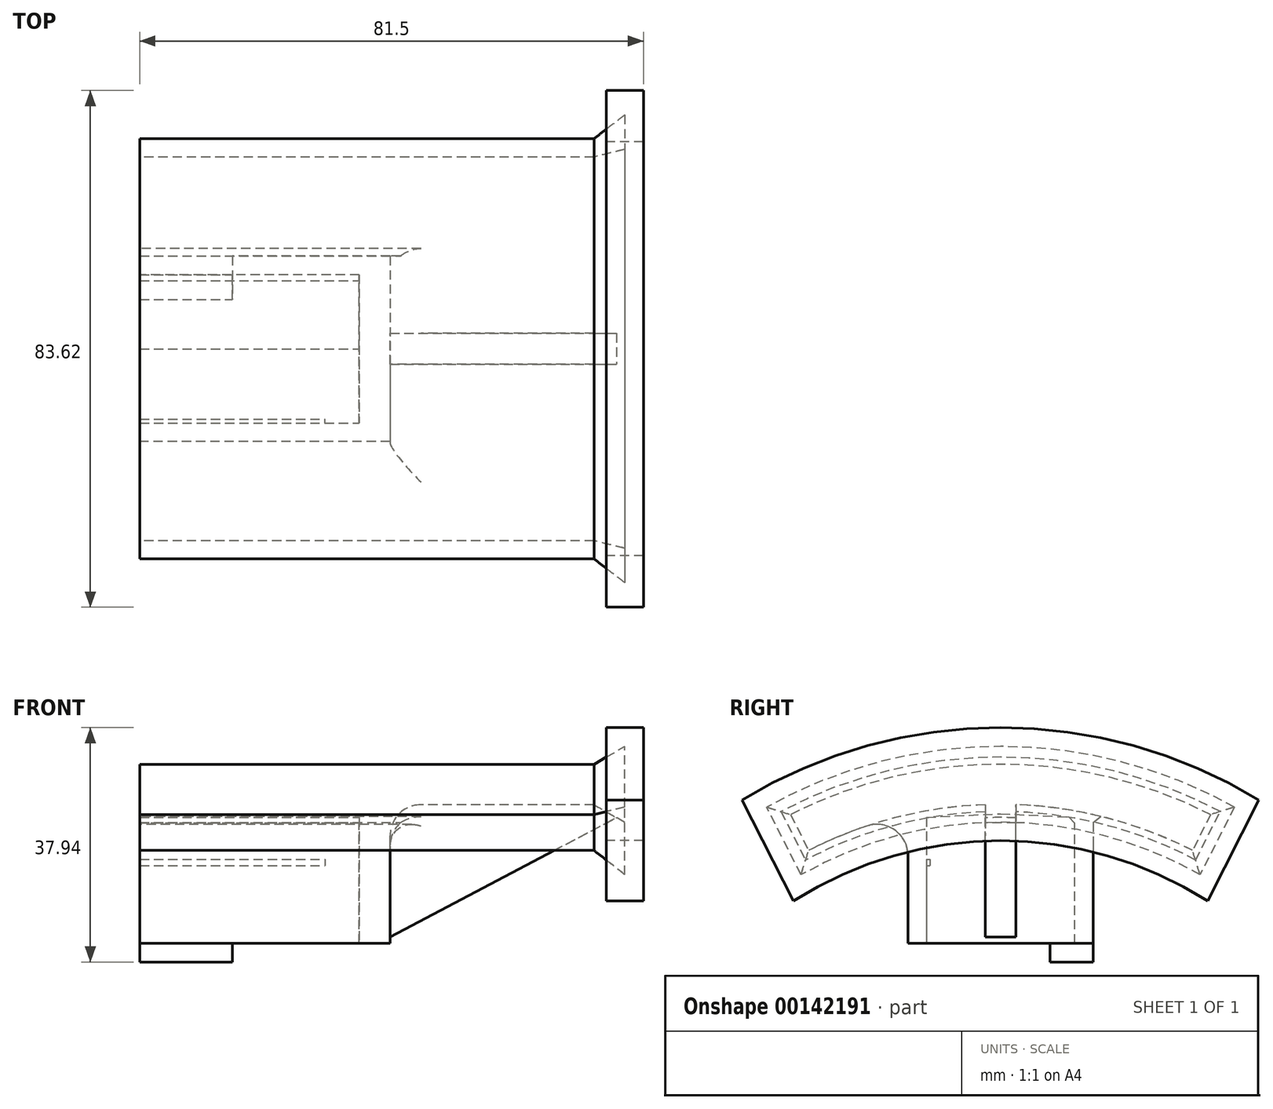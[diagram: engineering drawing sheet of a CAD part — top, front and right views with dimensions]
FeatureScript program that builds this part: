
annotation { "Feature Type Name" : "Feature", "Feature Type Description" : "" }
export const myFeature = defineFeature(function(context is Context, id is Id, definition is map)
    precondition{}
    {
        {
            var Q0;
            Q0=qCreatedBy(makeId("Right.planeOp"),FACE);
            var sketch = newSketch(context, id + "F0", { "sketchPlane" : qUnion([Q0])});
            skLineSegment(sketch, "E0", {"start": v(0, 0) * mm, "end": v(0, -27) * mm});
            skLineSegment(sketch, "E1", {"start": v(0, -27) * mm, "end": v(-7, -27) * mm});
            skLineSegment(sketch, "E2", {"start": v(-7, -27) * mm, "end": v(-7, -24) * mm});
            skLineSegment(sketch, "E3", {"start": v(-7, -24) * mm, "end": v(-3, -24) * mm});
            skLineSegment(sketch, "E4", {"start": v(-3, -24) * mm, "end": v(-3, -3) * mm});
            skLineSegment(sketch, "E5", {"start": v(-3, -3) * mm, "end": v(-27, -3) * mm});
            skLineSegment(sketch, "E6", {"start": v(-27, -3) * mm, "end": v(-27, -24) * mm});
            skLineSegment(sketch, "E7", {"start": v(-27, -24) * mm, "end": v(-30, -24) * mm});
            skLineSegment(sketch, "E8", {"start": v(-30, -24) * mm, "end": v(-30, 0) * mm});
            skLineSegment(sketch, "E9", {"start": v(-30, 0) * mm, "end": v(0, 0) * mm});
            skLineSegment(sketch, "E10.bottom", {"start": v(-27, -10.4) * mm, "end": v(-26.4, -10.4) * mm});
            skLineSegment(sketch, "E10.top", {"start": v(-27, -11.4) * mm, "end": v(-26.4, -11.4) * mm});
            skLineSegment(sketch, "E10.left", {"start": v(-27, -10.4) * mm, "end": v(-27, -11.4) * mm});
            skLineSegment(sketch, "E10.right", {"start": v(-26.4, -10.4) * mm, "end": v(-26.4, -11.4) * mm});
            skLineSegment(sketch, "E11", {"start": v(-3, -24) * mm, "end": v(0, -24) * mm});
            skLineSegment(sketch, "E12", {"start": v(-27, -3.6) * mm, "end": v(-15, -3) * mm});
            skLineSegment(sketch, "E13", {"start": v(-15, -3) * mm, "end": v(-3, -3.6) * mm});
            skSolve(sketch);
        }
        {
            var Q0;
            Q0=makeQuery(id+"F0.imprint","IMPRINT",FACE,{"disambiguationData":[TD([[makeQuery(id+"F0.imprint","IMPRINT",EDGE,{"derivedFrom":sQuery(id+"F0.wireOp",EDGE,"E0")}),-1.0]])]});
            var Q1;
            Q1=makeQuery(id+"F0.imprint","IMPRINT",FACE,{"disambiguationData":[TD([[makeQuery(id+"F0.imprint","IMPRINT",EDGE,{"derivedFrom":sQuery(id+"F0.wireOp",EDGE,"E10.bottom")}),-1.0]])]});
            var Q2;
            Q2=makeQuery(id+"F0.imprint","IMPRINT",FACE,{"disambiguationData":[TD([[makeQuery(id+"F0.imprint","IMPRINT",EDGE,{"derivedFrom":sQuery(id+"F0.wireOp",EDGE,"E4")}),-1.0]])]});
            var Q3;
            {var subQ3=sQuery(id+"F0.wireOp",EDGE,"E13");Q3=makeQuery(id+"F0.imprint","IMPRINT",FACE,{"disambiguationData":[TD([[makeQuery(id+"F0.imprint","IMPRINT",EDGE,{"derivedFrom":subQ3}),1.0]])]});}
            var Q4;
            {var subQ3=sQuery(id+"F0.wireOp",EDGE,"E12");Q4=makeQuery(id+"F0.imprint","IMPRINT",FACE,{"disambiguationData":[TD([[makeQuery(id+"F0.imprint","IMPRINT",EDGE,{"derivedFrom":subQ3}),1.0]])]});}
            extrude(context, id + "F1", {"entities" : qUnion([Q0, Q1, Q2, Q3, Q4]), "oppositeDirection" : true, "depth" : 15 * mm});
        }
        {
            var Q0;
            Q0=makeQuery(id+"F1.opExtrude","CAP_FACE",FACE,{"disambiguationData":[OSD([sQuery(id+"F0.wireOp",EDGE,"E0"),sQuery(id+"F0.wireOp",EDGE,"E1"),sQuery(id+"F0.wireOp",EDGE,"E2"),sQuery(id+"F0.wireOp",EDGE,"E3"),sQuery(id+"F0.wireOp",EDGE,"E4"),sQuery(id+"F0.wireOp",EDGE,"E5"),sQuery(id+"F0.wireOp",EDGE,"E6"),sQuery(id+"F0.wireOp",EDGE,"E7"),sQuery(id+"F0.wireOp",EDGE,"E8"),sQuery(id+"F0.wireOp",EDGE,"E9"),sQuery(id+"F0.wireOp",EDGE,"E10.bottom"),sQuery(id+"F0.wireOp",EDGE,"E10.top"),sQuery(id+"F0.wireOp",EDGE,"E10.right")])],"isStart":true});
            var sketch = newSketch(context, id + "F2", { "sketchPlane" : qUnion([Q0])});
            skLineSegment(sketch, "E14.bottom", {"start": v(-30, 0) * mm, "end": v(-27, 0) * mm});
            skLineSegment(sketch, "E14.top", {"start": v(-30, -24) * mm, "end": v(-27, -24) * mm});
            skLineSegment(sketch, "E14.left", {"start": v(-30, 0) * mm, "end": v(-30, -24) * mm});
            skLineSegment(sketch, "E14.right", {"start": v(-27, 0) * mm, "end": v(-27, -24) * mm});
            skLineSegment(sketch, "E15.bottom", {"start": v(0, 0) * mm, "end": v(-27, 0) * mm});
            skLineSegment(sketch, "E15.top", {"start": v(0, -24) * mm, "end": v(-27, -24) * mm});
            skLineSegment(sketch, "E15.left", {"start": v(0, 0) * mm, "end": v(0, -24) * mm});
            skLineSegment(sketch, "E16.bottom", {"start": v(0, -24) * mm, "end": v(-3, -24) * mm});
            skLineSegment(sketch, "E16.top", {"start": v(0, -24) * mm, "end": v(-3, -24) * mm});
            skLineSegment(sketch, "E16.left", {"start": v(0, -24) * mm, "end": v(0, -24) * mm});
            skLineSegment(sketch, "E16.right", {"start": v(-3, -24) * mm, "end": v(-3, -24) * mm});
            skSolve(sketch);
        }
        {
            var Q0;
            Q0=makeQuery(id+"F2.imprint","IMPRINT",FACE,{"disambiguationData":[TD([[makeQuery(id+"F2.imprint","IMPRINT",EDGE,{"derivedFrom":sQuery(id+"F2.wireOp",EDGE,"E14.bottom")}),-1.0]])]});
            var Q1;
            Q1=makeQuery(id+"F2.imprint","IMPRINT",FACE,{"disambiguationData":[TD([[makeQuery(id+"F2.imprint","IMPRINT",EDGE,{"derivedFrom":sQuery(id+"F2.wireOp",EDGE,"E15.bottom")}),-1.0]])]});
            extrude(context, id + "F3", {"entities" : qUnion([Q0, Q1]), "operationType" : NewBodyOperationType.ADD, "depth" : 20.5 * mm});
        }
        {
            var Q0;
            Q0=makeQuery(id+"F3.opExtrude","CAP_FACE",FACE,{"disambiguationData":[OSD([sQuery(id+"F2.wireOp",EDGE,"E14.bottom"),sQuery(id+"F2.wireOp",EDGE,"E14.top"),sQuery(id+"F2.wireOp",EDGE,"E14.left"),sQuery(id+"F2.wireOp",EDGE,"E14.right"),sQuery(id+"F2.wireOp",EDGE,"E15.bottom"),sQuery(id+"F2.wireOp",EDGE,"E15.top"),sQuery(id+"F2.wireOp",EDGE,"E15.left"),sQuery(id+"F2.wireOp",EDGE,"E16.bottom")])],"isStart":false});
            var sketch = newSketch(context, id + "F4", { "sketchPlane" : qUnion([Q0])});
            skLineSegment(sketch, "E17.bottom", {"start": v(-30, 0) * mm, "end": v(0, 0) * mm});
            skLineSegment(sketch, "E17.top", {"start": v(-30, -24) * mm, "end": v(0, -24) * mm});
            skLineSegment(sketch, "E17.left", {"start": v(-30, 0) * mm, "end": v(-30, -24) * mm});
            skLineSegment(sketch, "E17.right", {"start": v(0, 0) * mm, "end": v(0, -24) * mm});
            skSolve(sketch);
        }
        {
            var Q0;
            Q0 = qSketchRegion(id + "F4", true);
            extrude(context, id + "F5", {"entities" : qUnion([Q0]), "operationType" : NewBodyOperationType.ADD, "depth" : 5 * mm});
        }
        {
            var Q0;
            Q0=makeQuery(id+"F5.opExtrude","CAP_FACE",FACE,{"disambiguationData":[OSD([sQuery(id+"F4.wireOp",EDGE,"E17.bottom"),sQuery(id+"F4.wireOp",EDGE,"E17.top"),sQuery(id+"F4.wireOp",EDGE,"E17.left"),sQuery(id+"F4.wireOp",EDGE,"E17.right")])],"isStart":false});
            var sketch = newSketch(context, id + "F6", { "sketchPlane" : qUnion([Q0])});
            skCircle(sketch, "E18", {"center": v(-15, -70) * mm, "radius": 75 * mm});
            skCircle(sketch, "E19", {"center": v(-15, -70) * mm, "radius": 68.5 * mm});
            skLineSegment(sketch, "E20", {"start": v(-49, -3.15) * mm, "end": v(-15, -70) * mm});
            skLineSegment(sketch, "E21", {"start": v(19, -3.15) * mm, "end": v(-15, -70) * mm});
            skSolve(sketch);
        }
        {
            var Q0;
            {var subQ12=makeQuery(id+"F5.opExtrude","CAP_EDGE",EDGE,{"disambiguationData":[OSD([sQuery(id+"F4.wireOp",EDGE,"E17.bottom")])],"isStart":false});Q0=makeQuery(id+"F6.imprint","IMPRINT",FACE,{"disambiguationData":[TD([[makeQuery(id+"F6.imprint","IMPRINT",EDGE,{"derivedFrom":subQ12}),1.0]])]});}
            var Q1;
            {var subQ5=makeQuery(id+"F5.opExtrude","CAP_EDGE",EDGE,{"disambiguationData":[OSD([sQuery(id+"F4.wireOp",EDGE,"E17.bottom")])],"isStart":false});Q1=makeQuery(id+"F6.imprint","IMPRINT",FACE,{"disambiguationData":[TD([[makeQuery(id+"F6.imprint","IMPRINT",EDGE,{"derivedFrom":subQ5}),-1.0]])]});}
            var Q2;
            Q2=makeQuery(id+"F1.opExtrude","CAP_FACE",FACE,{"disambiguationData":[OSD([sQuery(id+"F0.wireOp",EDGE,"E0"),sQuery(id+"F0.wireOp",EDGE,"E1"),sQuery(id+"F0.wireOp",EDGE,"E2"),sQuery(id+"F0.wireOp",EDGE,"E3"),sQuery(id+"F0.wireOp",EDGE,"E4"),sQuery(id+"F0.wireOp",EDGE,"E5"),sQuery(id+"F0.wireOp",EDGE,"E6"),sQuery(id+"F0.wireOp",EDGE,"E7"),sQuery(id+"F0.wireOp",EDGE,"E8"),sQuery(id+"F0.wireOp",EDGE,"E9"),sQuery(id+"F0.wireOp",EDGE,"E10.bottom"),sQuery(id+"F0.wireOp",EDGE,"E10.top"),sQuery(id+"F0.wireOp",EDGE,"E10.right")])],"isStart":false});
            extrude(context, id + "F7", {"entities" : qUnion([Q0, Q1]), "operationType" : NewBodyOperationType.ADD, "depth" : 33 * mm, "hasSecondDirection" : true, "secondDirectionBound" : SecondDirectionBoundingType.UP_TO_SURFACE, "secondDirectionOppositeDirection" : true, "secondDirectionBoundEntityFace" : qUnion([Q2]), "secondDirectionDepth" : 25 * mm});
        }
        {
            var Q0;
            Q0=makeQuery(id+"F7.opExtrude","CAP_FACE",FACE,{"disambiguationData":[OSD([sQuery(id+"F6.wireOp",EDGE,"E18"),sQuery(id+"F6.wireOp",EDGE,"E19"),sQuery(id+"F6.wireOp",EDGE,"E20"),sQuery(id+"F6.wireOp",EDGE,"E21")])],"isStart":false});
            extrude(context, id + "F8", {"entities" : qUnion([Q0]), "operationType" : NewBodyOperationType.ADD, "depth" : 5 * mm, "hasDraft" : true, "draftAngle" : 30 * degree});
        }
        {
            var Q0;
            Q0=qCreatedBy(makeId("Front.planeOp"),FACE);
            var sketch = newSketch(context, id + "F9", { "sketchPlane" : qUnion([Q0])});
            skLineSegment(sketch, "E22", {"start": v(25.49, -22.98) * mm, "end": v(63.38, -2.98) * mm});
            skLineSegment(sketch, "E23", {"start": v(63.38, -2.98) * mm, "end": v(63.38, 0.02) * mm});
            skLineSegment(sketch, "E24", {"start": v(63.38, 0.02) * mm, "end": v(25.5, 0.02) * mm});
            skLineSegment(sketch, "E25", {"start": v(25.5, 0.02) * mm, "end": v(25.49, -22.98) * mm});
            skSolve(sketch);
        }
        {
            var Q0;
            Q0 = qSketchRegion(id + "F9", true);
            extrude(context, id + "F10", {"entities" : qUnion([Q0]), "depth" : 5 * mm});
        }
        {
            var Q0;
            Q0=makeQuery(id+"F10.opExtrude","SWEPT_BODY",BODY,{"disambiguationData":[OSD([sQuery(id+"F9.wireOp",EDGE,"E22"),sQuery(id+"F9.wireOp",EDGE,"E23"),sQuery(id+"F9.wireOp",EDGE,"E24"),sQuery(id+"F9.wireOp",EDGE,"E25")])]});
            var Q1;
            Q1=makeQuery(id+"F5.opExtrude","CAP_EDGE",EDGE,{"disambiguationData":[OSD([sQuery(id+"F4.wireOp",EDGE,"E17.top")])],"isStart":false});
            transform(context, id + "F11", {"entities" : qUnion([Q0]), "transformType" : TransformType.TRANSLATION_DISTANCE, "transformDirection" : qUnion([Q1]), "distance" : 12.5 * mm, "makeCopy" : false});
        }
        {
            var Q0;
            Q0=makeQuery(id+"F10.opExtrude","SWEPT_BODY",BODY,{"disambiguationData":[OSD([sQuery(id+"F9.wireOp",EDGE,"E22"),sQuery(id+"F9.wireOp",EDGE,"E23"),sQuery(id+"F9.wireOp",EDGE,"E24"),sQuery(id+"F9.wireOp",EDGE,"E25")])]});
            var Q1;
            Q1=makeQuery(id+"F1.opExtrude","SWEPT_BODY",BODY,{"disambiguationData":[OSD([sQuery(id+"F0.wireOp",EDGE,"E0"),sQuery(id+"F0.wireOp",EDGE,"E1"),sQuery(id+"F0.wireOp",EDGE,"E2"),sQuery(id+"F0.wireOp",EDGE,"E3"),sQuery(id+"F0.wireOp",EDGE,"E4"),sQuery(id+"F0.wireOp",EDGE,"E5"),sQuery(id+"F0.wireOp",EDGE,"E6"),sQuery(id+"F0.wireOp",EDGE,"E7"),sQuery(id+"F0.wireOp",EDGE,"E8"),sQuery(id+"F0.wireOp",EDGE,"E9"),sQuery(id+"F0.wireOp",EDGE,"E10.bottom"),sQuery(id+"F0.wireOp",EDGE,"E10.top"),sQuery(id+"F0.wireOp",EDGE,"E10.right")])]});
            booleanBodies(context, id + "F12", {"operationType" : BooleanOperationType.UNION, "tools" : qUnion([Q0, Q1])});
        }
        {
            var Q0;
            Q0=makeQuery(id+"F7.boolean.opBoolean","INTERSECT",EDGE,{"derivedFrom":[makeQuery(id+"F5.boolean.opBoolean","MERGE",FACE,{"derivedFrom":[makeQuery(id+"F3.boolean.opBoolean","MERGE",FACE,{"derivedFrom":[makeQuery(id+"F1.opExtrude","SWEPT_FACE",FACE,{"disambiguationData":[OSD([sQuery(id+"F0.wireOp",EDGE,"E8")])]}),makeQuery(id+"F3.opExtrude","SWEPT_FACE",FACE,{"disambiguationData":[OSD([sQuery(id+"F2.wireOp",EDGE,"E14.left")])]})]}),makeQuery(id+"F5.opExtrude","SWEPT_FACE",FACE,{"disambiguationData":[OSD([sQuery(id+"F4.wireOp",EDGE,"E17.left")])]})]}),makeQuery(id+"F7.opExtrude","SWEPT_FACE",FACE,{"disambiguationData":[OSD([sQuery(id+"F6.wireOp",EDGE,"E19")])]})]});
            var Q1;
            {var subQ0=sQuery(id+"F4.wireOp",EDGE,"E17.right");var subQ1=makeQuery(id+"F5.opExtrude","CAP_FACE",FACE,{"disambiguationData":[OSD([sQuery(id+"F4.wireOp",EDGE,"E17.bottom"),sQuery(id+"F4.wireOp",EDGE,"E17.top"),sQuery(id+"F4.wireOp",EDGE,"E17.left"),subQ0])],"isStart":false});var subQ2=makeQuery(id+"F7.opExtrude","SWEPT_FACE",FACE,{"disambiguationData":[OSD([sQuery(id+"F6.wireOp",EDGE,"E19")])]});Q1=makeQuery(id+"F12.opBoolean","SPLIT",EDGE,{"disambiguationData":[TD([makeQuery(id+"F1.opExtrude","SWEPT_FACE",FACE,{"disambiguationData":[OSD([sQuery(id+"F0.wireOp",EDGE,"E0")])]})])],"derivedFrom":makeQuery(id+"F7.boolean.opBoolean","INTERSECT",EDGE,{"derivedFrom":[subQ1,subQ2]})});}
            var Q2;
            {var subQ0=sQuery(id+"F4.wireOp",EDGE,"E17.left");var subQ1=makeQuery(id+"F5.opExtrude","CAP_FACE",FACE,{"disambiguationData":[OSD([sQuery(id+"F4.wireOp",EDGE,"E17.bottom"),sQuery(id+"F4.wireOp",EDGE,"E17.top"),subQ0,sQuery(id+"F4.wireOp",EDGE,"E17.right")])],"isStart":false});var subQ2=makeQuery(id+"F7.opExtrude","SWEPT_FACE",FACE,{"disambiguationData":[OSD([sQuery(id+"F6.wireOp",EDGE,"E19")])]});Q2=makeQuery(id+"F12.opBoolean","SPLIT",EDGE,{"disambiguationData":[TD([makeQuery(id+"F1.opExtrude","SWEPT_FACE",FACE,{"disambiguationData":[OSD([sQuery(id+"F0.wireOp",EDGE,"E8")])]})])],"derivedFrom":makeQuery(id+"F7.boolean.opBoolean","INTERSECT",EDGE,{"derivedFrom":[subQ1,subQ2]})});}
            fillet(context, id + "F13", {"entities" : qUnion([Q0, Q1, Q2]), "radius" : 5 * mm, "tangentPropagation" : true, "allowEdgeOverflow" : false});
        }
        {
            var Q0;
            Q0=makeQuery(id+"F7.boolean.opBoolean","INTERSECT",EDGE,{"derivedFrom":[makeQuery(id+"F5.boolean.opBoolean","MERGE",FACE,{"derivedFrom":[makeQuery(id+"F3.boolean.opBoolean","MERGE",FACE,{"derivedFrom":[makeQuery(id+"F1.opExtrude","SWEPT_FACE",FACE,{"disambiguationData":[OSD([sQuery(id+"F0.wireOp",EDGE,"E0")])]}),makeQuery(id+"F3.opExtrude","SWEPT_FACE",FACE,{"disambiguationData":[OSD([sQuery(id+"F2.wireOp",EDGE,"E15.left")])]})]}),makeQuery(id+"F5.opExtrude","SWEPT_FACE",FACE,{"disambiguationData":[OSD([sQuery(id+"F4.wireOp",EDGE,"E17.right")])]})]}),makeQuery(id+"F7.opExtrude","SWEPT_FACE",FACE,{"disambiguationData":[OSD([sQuery(id+"F6.wireOp",EDGE,"E19")])]})]});
            chamfer(context, id + "F14", {"entities" : qUnion([Q0]), "width" : 1 * mm, "tangentPropagation" : true});
        }
        {
            var Q0;
            Q0=makeQuery(id+"FxV5dlsvzGUwSKC_2.boolean.opBoolean","MERGE",EDGE,{"derivedFrom":[makeQuery(id+"F1.opExtrude","SWEPT_EDGE",EDGE,{"disambiguationData":[OSD([sQuery(id+"F0.wireOp",EDGE,"E4"),sQuery(id+"F0.wireOp",EDGE,"E5")])]}),makeQuery(id+"FxV5dlsvzGUwSKC_2.opExtrude","SWEPT_EDGE",EDGE,{"disambiguationData":[OSD([sQuery(id+"FTIyNGWiZXPathp_2.wireOp",EDGE,"jA4ZDa5l-lHbp-5HIl-XP0d-kzFAkvVPCaqd.top"),sQuery(id+"FTIyNGWiZXPathp_2.wireOp",EDGE,"jA4ZDa5l-lHbp-5HIl-XP0d-kzFAkvVPCaqd.left")])]})]});
            chamfer(context, id + "F15", {"entities" : qUnion([Q0]), "width" : 1 * mm, "tangentPropagation" : true});
        }
        {
            var Q0;
            {var subQ0=sQuery(id+"F0.wireOp",EDGE,"E7");var subQ1=sQuery(id+"F0.wireOp",EDGE,"E6");var subQ3=sQuery(id+"F0.wireOp",EDGE,"E10.top");var subQ4=sQuery(id+"F0.wireOp",EDGE,"E10.bottom");var subQ5=sQuery(id+"F0.wireOp",EDGE,"E12");var subQ6=sQuery(id+"F0.wireOp",EDGE,"E10.right");Q0=makeQuery(id+"F3.boolean.opBoolean","SPLIT",FACE,{"disambiguationData":[TD([makeQuery(id+"F1.opExtrude","SWEPT_FACE",FACE,{"disambiguationData":[OSD([subQ4])]})])],"derivedFrom":makeQuery(id+"F1.opExtrude","CAP_FACE",FACE,{"disambiguationData":[OSD([sQuery(id+"F0.wireOp",EDGE,"E0"),sQuery(id+"F0.wireOp",EDGE,"E1"),sQuery(id+"F0.wireOp",EDGE,"E2"),sQuery(id+"F0.wireOp",EDGE,"E3"),sQuery(id+"F0.wireOp",EDGE,"E4"),subQ1,subQ0,sQuery(id+"F0.wireOp",EDGE,"E8"),sQuery(id+"F0.wireOp",EDGE,"E9"),subQ4,subQ3,subQ6,subQ5,sQuery(id+"F0.wireOp",EDGE,"E13")])],"isStart":true})});}
            extrude(context, id + "F16", {"entities" : qUnion([Q0]), "operationType" : NewBodyOperationType.ADD, "depth" : 15 * mm});
        }
        {
            var Q0;
            Q0=makeQuery(id+"F8.opExtrude","CAP_FACE",FACE,{"disambiguationData":[OSD([sQuery(id+"F6.wireOp",EDGE,"E18"),sQuery(id+"F6.wireOp",EDGE,"E19"),sQuery(id+"F6.wireOp",EDGE,"E20"),sQuery(id+"F6.wireOp",EDGE,"E21")])],"isStart":false});
            var sketch = newSketch(context, id + "F17", { "sketchPlane" : qUnion([Q0])});
            skArc(sketch, "E26.0", {"start": v(26.81, -0.77) * mm, "mid": v(-15, 10.94) * mm, "end": v(-56.81, -0.77) * mm});
            skLineSegment(sketch, "E26.1", {"start": v(18.5, -17.11) * mm, "end": v(26.81, -0.77) * mm});
            skArc(sketch, "E26.2", {"start": v(18.5, -17.11) * mm, "mid": v(-15, -7.36) * mm, "end": v(-48.5, -17.11) * mm});
            skLineSegment(sketch, "E26.3", {"start": v(-56.81, -0.77) * mm, "end": v(-48.5, -17.11) * mm});
            skSolve(sketch);
        }
        {
            var Q0;
            Q0=makeQuery(id+"F17.imprint","IMPRINT",FACE,{"disambiguationData":[TD([[makeQuery(id+"F17.imprint","IMPRINT",EDGE,{"derivedFrom":sQuery(id+"F17.wireOp",EDGE,"E26.0")}),1.0]])]});
            var sketch = newSketch(context, id + "F18", { "sketchPlane" : qUnion([Q0])});
            skArc(sketch, "E27.0", {"start": v(26.81, -0.77) * mm, "mid": v(-15, 10.94) * mm, "end": v(-56.81, -0.77) * mm});
            skLineSegment(sketch, "E27.1", {"start": v(-56.81, -0.77) * mm, "end": v(-48.5, -17.11) * mm});
            skArc(sketch, "E27.2", {"start": v(18.5, -17.11) * mm, "mid": v(-15, -7.36) * mm, "end": v(-48.5, -17.11) * mm});
            skLineSegment(sketch, "E27.3", {"start": v(18.5, -17.11) * mm, "end": v(26.81, -0.77) * mm});
            skSolve(sketch);
        }
        {
            var Q0;
            Q0 = qSketchRegion(id + "F18", true);
            extrude(context, id + "F19", {"entities" : qUnion([Q0]), "endBound" : BoundingType.SYMMETRIC, "depth" : 6 * mm});
        }
        {
            var Q0;
            Q0=makeQuery(id+"F10.opExtrude","SWEPT_BODY",BODY,{"disambiguationData":[OSD([sQuery(id+"F9.wireOp",EDGE,"E22"),sQuery(id+"F9.wireOp",EDGE,"E23"),sQuery(id+"F9.wireOp",EDGE,"E24"),sQuery(id+"F9.wireOp",EDGE,"E25")])]});
            var Q1;
            Q1=makeQuery(id+"F19.opExtrude","SWEPT_BODY",BODY,{"disambiguationData":[OSD([sQuery(id+"F18.wireOp",EDGE,"E27.0"),sQuery(id+"F18.wireOp",EDGE,"E27.1"),sQuery(id+"F18.wireOp",EDGE,"E27.2"),sQuery(id+"F18.wireOp",EDGE,"E27.3")])]});
            booleanBodies(context, id + "F20", {"operationType" : BooleanOperationType.SUBTRACTION, "tools" : qUnion([Q0]), "targets" : qUnion([Q1]), "keepTools" : true});
        }
    });
